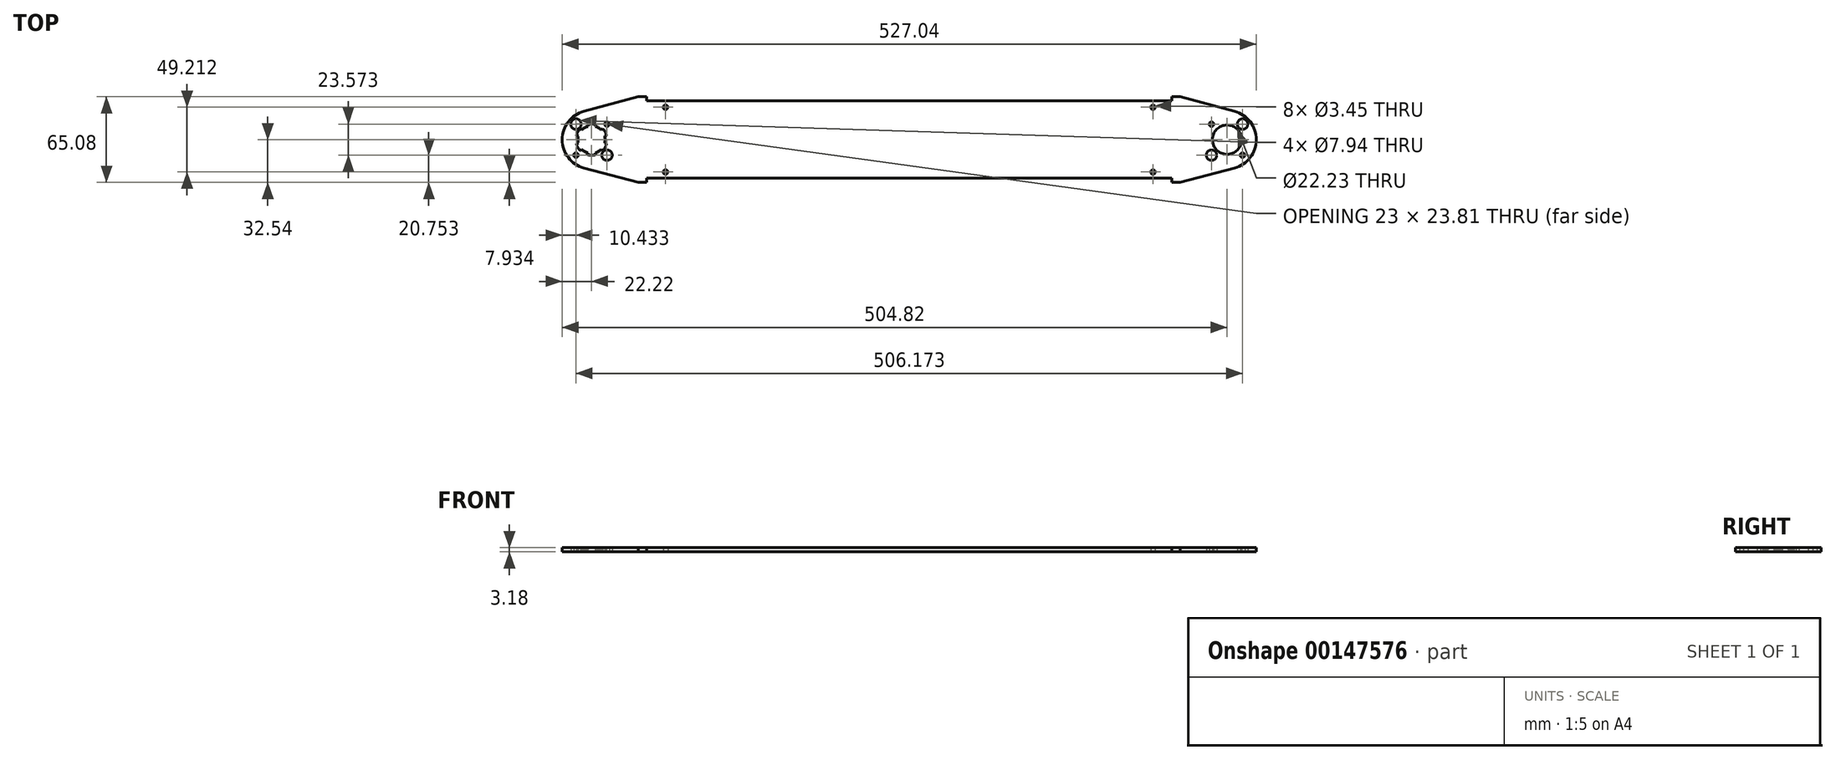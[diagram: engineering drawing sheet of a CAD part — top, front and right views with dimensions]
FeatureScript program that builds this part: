
annotation { "Feature Type Name" : "Feature", "Feature Type Description" : "" }
export const myFeature = defineFeature(function(context is Context, id is Id, definition is map)
    precondition{}
    {
        {
            var Q0;
            Q0=qCreatedBy(makeId("Top.planeOp"),FACE);
            var sketch = newSketch(context, id + "F0", { "sketchPlane" : qUnion([Q0])});
            skPoint(sketch, "E0.rect.middle", {"position": v(0, 0) * mm});
            skCircle(sketch, "E1", {"center": v(0, 0) * mm, "radius": 11.11 * mm});
            skLineSegment(sketch, "E2.bottom", {"start": v(11.79, 11.79) * mm, "end": v(-11.79, 11.79) * mm, "construction": true});
            skLineSegment(sketch, "E2.left", {"start": v(11.79, 11.79) * mm, "end": v(11.79, -11.79) * mm, "construction": true});
            skLineSegment(sketch, "E2.right", {"start": v(-11.79, 11.79) * mm, "end": v(-11.79, -11.79) * mm, "construction": true});
            skCircle(sketch, "E3", {"center": v(11.79, 11.79) * mm, "radius": 5.56 * mm, "construction": true});
            skCircle(sketch, "E4", {"center": v(-11.79, 11.79) * mm, "radius": 1.73 * mm});
            skCircle(sketch, "E5", {"center": v(11.79, 11.79) * mm, "radius": 3.97 * mm});
            skCircle(sketch, "E6", {"center": v(11.79, -11.79) * mm, "radius": 1.73 * mm});
            skCircle(sketch, "E7", {"center": v(-11.79, -11.79) * mm, "radius": 3.97 * mm});
            skArc(sketch, "E8", {"start": v(-488.35, 21.47) * mm, "mid": v(-504.83, 0) * mm, "end": v(-488.35, -21.47) * mm});
            skLineSegment(sketch, "E9.bottom", {"start": v(-494.39, 11.79) * mm, "end": v(-470.81, 11.79) * mm, "construction": true});
            skLineSegment(sketch, "E9.top", {"start": v(-494.39, -11.79) * mm, "end": v(-470.81, -11.79) * mm, "construction": true});
            skLineSegment(sketch, "E9.left", {"start": v(-494.39, 11.79) * mm, "end": v(-494.39, -11.79) * mm, "construction": true});
            skLineSegment(sketch, "E9.right", {"start": v(-470.81, 11.79) * mm, "end": v(-470.81, -11.79) * mm, "construction": true});
            skCircle(sketch, "E10", {"center": v(-470.81, 11.79) * mm, "radius": 1.73 * mm});
            skCircle(sketch, "E11", {"center": v(-482.6, 0) * mm, "radius": 10.32 * mm});
            skCircle(sketch, "E12", {"center": v(-494.39, 11.79) * mm, "radius": 3.97 * mm});
            skCircle(sketch, "E13", {"center": v(-494.39, -11.79) * mm, "radius": 1.73 * mm});
            skCircle(sketch, "E14", {"center": v(-470.81, -11.79) * mm, "radius": 3.97 * mm});
            skLineSegment(sketch, "E15", {"start": v(0, 0) * mm, "end": v(-482.6, 0) * mm, "construction": true});
            skLineSegment(sketch, "E16", {"start": v(-488.35, -21.47) * mm, "end": v(-447.02, -32.54) * mm});
            skLineSegment(sketch, "E17", {"start": v(-488.35, 21.47) * mm, "end": v(-447.02, 32.54) * mm});
            skLineSegment(sketch, "E18", {"start": v(-440.67, -29.37) * mm, "end": v(-41.93, -29.37) * mm});
            skLineSegment(sketch, "E19", {"start": v(-440.67, 29.37) * mm, "end": v(-41.93, 29.37) * mm});
            skLineSegment(sketch, "E20", {"start": v(-440.67, 32.54) * mm, "end": v(-440.67, 29.37) * mm});
            skLineSegment(sketch, "E21", {"start": v(-440.67, 32.54) * mm, "end": v(-447.02, 32.54) * mm});
            skLineSegment(sketch, "E22", {"start": v(-440.67, -29.37) * mm, "end": v(-440.67, -32.54) * mm});
            skLineSegment(sketch, "E23", {"start": v(-440.67, -32.54) * mm, "end": v(-447.02, -32.54) * mm});
            skLineSegment(sketch, "E24", {"start": v(-41.93, -29.37) * mm, "end": v(-41.93, -32.54) * mm});
            skLineSegment(sketch, "E25", {"start": v(-41.93, -32.54) * mm, "end": v(-35.58, -32.54) * mm});
            skLineSegment(sketch, "E26", {"start": v(-41.93, 29.37) * mm, "end": v(-41.93, 32.54) * mm});
            skLineSegment(sketch, "E27", {"start": v(-41.93, 32.54) * mm, "end": v(-35.58, 32.54) * mm});
            skLineSegment(sketch, "E28", {"start": v(-35.58, -32.54) * mm, "end": v(5.75, -21.47) * mm});
            skLineSegment(sketch, "E29", {"start": v(5.75, 21.47) * mm, "end": v(-35.58, 32.54) * mm});
            skArc(sketch, "E30", {"start": v(5.75, -21.47) * mm, "mid": v(22.23, 0) * mm, "end": v(5.75, 21.47) * mm});
            skLineSegment(sketch, "E31", {"start": v(-440.67, 29.37) * mm, "end": v(-440.67, 24.6) * mm, "construction": true});
            skLineSegment(sketch, "E32", {"start": v(-440.67, 24.6) * mm, "end": v(-426.38, 24.6) * mm, "construction": true});
            skLineSegment(sketch, "E33", {"start": v(-440.67, -29.37) * mm, "end": v(-440.67, -24.6) * mm, "construction": true});
            skLineSegment(sketch, "E34", {"start": v(-440.67, -24.6) * mm, "end": v(-426.38, -24.6) * mm, "construction": true});
            skLineSegment(sketch, "E35", {"start": v(-41.93, -29.37) * mm, "end": v(-41.93, -24.6) * mm, "construction": true});
            skLineSegment(sketch, "E36", {"start": v(-41.93, -24.6) * mm, "end": v(-56.22, -24.6) * mm, "construction": true});
            skLineSegment(sketch, "E37", {"start": v(-41.93, 29.37) * mm, "end": v(-41.93, 24.6) * mm, "construction": true});
            skLineSegment(sketch, "E38", {"start": v(-41.93, 24.6) * mm, "end": v(-56.22, 24.6) * mm, "construction": true});
            skCircle(sketch, "E39", {"center": v(-426.38, 24.6) * mm, "radius": 1.73 * mm});
            skCircle(sketch, "E40", {"center": v(-56.22, 24.6) * mm, "radius": 1.73 * mm});
            skCircle(sketch, "E41", {"center": v(-56.22, -24.6) * mm, "radius": 1.73 * mm});
            skCircle(sketch, "E42", {"center": v(-426.38, -24.6) * mm, "radius": 1.73 * mm});
            skLineSegment(sketch, "E43", {"start": v(-11.79, -11.79) * mm, "end": v(11.79, -11.79) * mm, "construction": true});
            skLineSegment(sketch, "E44", {"start": v(-241.3, -29.37) * mm, "end": v(-241.3, 0) * mm, "construction": true});
            skLineSegment(sketch, "E45", {"start": v(-241.3, 0) * mm, "end": v(-241.3, 29.37) * mm, "construction": true});
            skSolve(sketch);
        }
        {
            var Q0;
            Q0=qSketchRegion(id+"F0",true);
            extrude(context, id + "F1", {"entities" : qUnion([Q0]), "depth" : 3.17 * mm});
        }
        {
            var Q0;
            Q0=makeQuery(id+"F1.opExtrude","CAP_FACE",FACE,{"disambiguationData":[OSD([sQuery(id+"F0.wireOp",EDGE,"d63eafa0-1946-4b0e-8293-95e246b273c5.rect.bottom"),sQuery(id+"F0.wireOp",EDGE,"d63eafa0-1946-4b0e-8293-95e246b273c5.rect.top"),sQuery(id+"F0.wireOp",EDGE,"5983dcdd-59a7-4b72-80fd-e4567be1ae8a"),sQuery(id+"F0.wireOp",EDGE,"5a538b3e-fc2b-4d64-affd-5d60433388e5"),sQuery(id+"F0.wireOp",EDGE,"72e86de7-b207-474f-aadf-64543fae3f9b"),sQuery(id+"F0.wireOp",EDGE,"1c038800-5bd5-4753-8b38-6da13ef78ef9"),sQuery(id+"F0.wireOp",EDGE,"EbMUZoU6-Ffds-1dNq-SxhE-hPi8oSjhvaod"),sQuery(id+"F0.wireOp",EDGE,"RfgQjzcw-1Izs-lnTa-bWkk-oBHRDQjbZqQC"),sQuery(id+"F0.wireOp",EDGE,"1cCQAcjj-TyQA-3DMx-kDix-v5yZVaaGeXVM"),sQuery(id+"F0.wireOp",EDGE,"7KPu8lni-3ZWA-t6oJ-FRoh-C5MB3aVr7E9B"),sQuery(id+"F0.wireOp",EDGE,"bSzr06ES-7M0i-Fw5H-UJmt-4e4EQGRPIe4n"),sQuery(id+"F0.wireOp",EDGE,"WGsr6OjU-OX8l-mawA-7cCc-MfOuMOY06Cp5"),sQuery(id+"F0.wireOp",EDGE,"9mrz1cDN-18gM-20ra-6VCO-jp25g10tvNn2"),sQuery(id+"F0.wireOp",EDGE,"G0uOisy3-Mq6h-PcKh-Zkf4-CVoCvP3Hii1l"),sQuery(id+"F0.wireOp",EDGE,"1ae556be-0ab9-4322-b48e-98cf5a741ae0"),sQuery(id+"F0.wireOp",EDGE,"676cd913-43f8-42b3-8cdc-a90136d19ef5"),sQuery(id+"F0.wireOp",EDGE,"xnt2EyF8-ZVyQ-RbWD-GIsP-ThkcyX8ZioIH.bottom"),sQuery(id+"F0.wireOp",EDGE,"xnt2EyF8-ZVyQ-RbWD-GIsP-ThkcyX8ZioIH.top"),sQuery(id+"F0.wireOp",EDGE,"xnt2EyF8-ZVyQ-RbWD-GIsP-ThkcyX8ZioIH.left"),sQuery(id+"F0.wireOp",EDGE,"E1"),sQuery(id+"F0.wireOp",EDGE,"Jo9pZc7T-t0kF-vjz1-dNbX-L65bwNqtrrdz"),sQuery(id+"F0.wireOp",EDGE,"lEYoY9t7-PMOS-SVp6-xfnB-Xp9WdWMCDdum"),sQuery(id+"F0.wireOp",EDGE,"s7aM02SC-9XQ7-dueL-DqMg-ZFuJqOofj9mt"),sQuery(id+"F0.wireOp",EDGE,"deKa9ngt-XMq2-GGkr-SZIa-KlyN0U5bcCDe"),sQuery(id+"F0.wireOp",EDGE,"E4"),sQuery(id+"F0.wireOp",EDGE,"E5"),sQuery(id+"F0.wireOp",EDGE,"E6"),sQuery(id+"F0.wireOp",EDGE,"E7"),sQuery(id+"F0.wireOp",EDGE,"E8"),sQuery(id+"F0.wireOp",EDGE,"E10"),sQuery(id+"F0.wireOp",EDGE,"E11"),sQuery(id+"F0.wireOp",EDGE,"E12"),sQuery(id+"F0.wireOp",EDGE,"E13"),sQuery(id+"F0.wireOp",EDGE,"E14")])],"isStart":true});
            var sketch = newSketch(context, id + "F2", { "sketchPlane" : qUnion([Q0])});
            skLineSegment(sketch, "E46", {"start": v(-482.6, 0) * mm, "end": v(-491.54, -5.16) * mm, "construction": true});
            skArc(sketch, "E47", {"start": v(-492.57, -2.67) * mm, "mid": v(-491.54, -5.16) * mm, "end": v(-489.9, -7.3) * mm});
            skLineSegment(sketch, "E48", {"start": v(-482.6, 0) * mm, "end": v(-489.9, -7.3) * mm, "construction": true});
            skLineSegment(sketch, "E49", {"start": v(-482.6, 0) * mm, "end": v(-492.57, -2.67) * mm, "construction": true});
            skLineSegment(sketch, "E50", {"start": v(-489.9, -7.3) * mm, "end": v(-491.02, -8.42) * mm});
            skLineSegment(sketch, "E51", {"start": v(-492.57, -2.67) * mm, "end": v(-494.1, -3.08) * mm});
            skArc(sketch, "E52", {"start": v(-494.1, -3.08) * mm, "mid": v(-492.91, -5.95) * mm, "end": v(-491.02, -8.42) * mm});
            skLineSegment(sketch, "E53", {"start": v(-482.6, 0) * mm, "end": v(-492.92, 0) * mm, "construction": true});
            skSolve(sketch);
        }
        {
            var Q0;
            Q0=qSketchRegion(id+"F2",true);
            var Q1;
            Q1=makeQuery(id+"F1.opExtrude","CAP_FACE",FACE,{"disambiguationData":[OSD([sQuery(id+"F0.wireOp",EDGE,"d63eafa0-1946-4b0e-8293-95e246b273c5.rect.bottom"),sQuery(id+"F0.wireOp",EDGE,"d63eafa0-1946-4b0e-8293-95e246b273c5.rect.top"),sQuery(id+"F0.wireOp",EDGE,"5983dcdd-59a7-4b72-80fd-e4567be1ae8a"),sQuery(id+"F0.wireOp",EDGE,"5a538b3e-fc2b-4d64-affd-5d60433388e5"),sQuery(id+"F0.wireOp",EDGE,"72e86de7-b207-474f-aadf-64543fae3f9b"),sQuery(id+"F0.wireOp",EDGE,"1c038800-5bd5-4753-8b38-6da13ef78ef9"),sQuery(id+"F0.wireOp",EDGE,"EbMUZoU6-Ffds-1dNq-SxhE-hPi8oSjhvaod"),sQuery(id+"F0.wireOp",EDGE,"RfgQjzcw-1Izs-lnTa-bWkk-oBHRDQjbZqQC"),sQuery(id+"F0.wireOp",EDGE,"1cCQAcjj-TyQA-3DMx-kDix-v5yZVaaGeXVM"),sQuery(id+"F0.wireOp",EDGE,"7KPu8lni-3ZWA-t6oJ-FRoh-C5MB3aVr7E9B"),sQuery(id+"F0.wireOp",EDGE,"bSzr06ES-7M0i-Fw5H-UJmt-4e4EQGRPIe4n"),sQuery(id+"F0.wireOp",EDGE,"WGsr6OjU-OX8l-mawA-7cCc-MfOuMOY06Cp5"),sQuery(id+"F0.wireOp",EDGE,"9mrz1cDN-18gM-20ra-6VCO-jp25g10tvNn2"),sQuery(id+"F0.wireOp",EDGE,"G0uOisy3-Mq6h-PcKh-Zkf4-CVoCvP3Hii1l"),sQuery(id+"F0.wireOp",EDGE,"1ae556be-0ab9-4322-b48e-98cf5a741ae0"),sQuery(id+"F0.wireOp",EDGE,"676cd913-43f8-42b3-8cdc-a90136d19ef5"),sQuery(id+"F0.wireOp",EDGE,"xnt2EyF8-ZVyQ-RbWD-GIsP-ThkcyX8ZioIH.bottom"),sQuery(id+"F0.wireOp",EDGE,"xnt2EyF8-ZVyQ-RbWD-GIsP-ThkcyX8ZioIH.top"),sQuery(id+"F0.wireOp",EDGE,"xnt2EyF8-ZVyQ-RbWD-GIsP-ThkcyX8ZioIH.left"),sQuery(id+"F0.wireOp",EDGE,"E1"),sQuery(id+"F0.wireOp",EDGE,"Jo9pZc7T-t0kF-vjz1-dNbX-L65bwNqtrrdz"),sQuery(id+"F0.wireOp",EDGE,"lEYoY9t7-PMOS-SVp6-xfnB-Xp9WdWMCDdum"),sQuery(id+"F0.wireOp",EDGE,"s7aM02SC-9XQ7-dueL-DqMg-ZFuJqOofj9mt"),sQuery(id+"F0.wireOp",EDGE,"deKa9ngt-XMq2-GGkr-SZIa-KlyN0U5bcCDe"),sQuery(id+"F0.wireOp",EDGE,"E4"),sQuery(id+"F0.wireOp",EDGE,"E5"),sQuery(id+"F0.wireOp",EDGE,"E6"),sQuery(id+"F0.wireOp",EDGE,"E7"),sQuery(id+"F0.wireOp",EDGE,"E8"),sQuery(id+"F0.wireOp",EDGE,"E10"),sQuery(id+"F0.wireOp",EDGE,"E11"),sQuery(id+"F0.wireOp",EDGE,"E12"),sQuery(id+"F0.wireOp",EDGE,"E13"),sQuery(id+"F0.wireOp",EDGE,"E14")])],"isStart":false});
            extrude(context, id + "F3", {"entities" : qUnion([Q0]), "operationType" : NewBodyOperationType.REMOVE, "endBound" : BoundingType.UP_TO_SURFACE, "oppositeDirection" : true, "endBoundEntityFace" : qUnion([Q1]), "depth" : 25.4 * mm});
        }
        {
            var Q0;
            Q0=makeQuery(id+"F3.boolean.opBoolean","COPY",FACE,{"derivedFrom":makeQuery(id+"F3.opExtrude","SWEPT_FACE",FACE,{"disambiguationData":[OSD([sQuery(id+"F2.wireOp",EDGE,"E50")])]})});
            var Q1;
            Q1=makeQuery(id+"F3.boolean.opBoolean","COPY",FACE,{"derivedFrom":makeQuery(id+"F3.opExtrude","SWEPT_FACE",FACE,{"disambiguationData":[OSD([sQuery(id+"F2.wireOp",EDGE,"E52")])]})});
            var Q2;
            Q2=makeQuery(id+"F3.boolean.opBoolean","COPY",FACE,{"derivedFrom":makeQuery(id+"F3.opExtrude","SWEPT_FACE",FACE,{"disambiguationData":[OSD([sQuery(id+"F2.wireOp",EDGE,"E51")])]})});
            var Q3;
            Q3=makeQuery(id+"F1.opExtrude","SWEPT_FACE",FACE,{"disambiguationData":[OSD([sQuery(id+"F0.wireOp",EDGE,"E11")])]});
            circularPattern(context, id + "F4", {"patternType" : PatternType.FACE, "faces" : qUnion([Q0, Q1, Q2]), "axis" : qUnion([Q3]), "angle" : 60 * degree, "instanceCount" : 6});
        }
        {
            var Q0;
            Q0=makeQuery(id+"F1.opExtrude","CAP_FACE",FACE,{"disambiguationData":[OSD([sQuery(id+"F0.wireOp",EDGE,"E1"),sQuery(id+"F0.wireOp",EDGE,"E4"),sQuery(id+"F0.wireOp",EDGE,"E5"),sQuery(id+"F0.wireOp",EDGE,"E6"),sQuery(id+"F0.wireOp",EDGE,"E7"),sQuery(id+"F0.wireOp",EDGE,"E8"),sQuery(id+"F0.wireOp",EDGE,"E10"),sQuery(id+"F0.wireOp",EDGE,"E11"),sQuery(id+"F0.wireOp",EDGE,"E12"),sQuery(id+"F0.wireOp",EDGE,"E13"),sQuery(id+"F0.wireOp",EDGE,"E14"),sQuery(id+"F0.wireOp",EDGE,"E16"),sQuery(id+"F0.wireOp",EDGE,"E17"),sQuery(id+"F0.wireOp",EDGE,"E18"),sQuery(id+"F0.wireOp",EDGE,"E19"),sQuery(id+"F0.wireOp",EDGE,"E20"),sQuery(id+"F0.wireOp",EDGE,"E21"),sQuery(id+"F0.wireOp",EDGE,"E22"),sQuery(id+"F0.wireOp",EDGE,"E23"),sQuery(id+"F0.wireOp",EDGE,"E24"),sQuery(id+"F0.wireOp",EDGE,"E25"),sQuery(id+"F0.wireOp",EDGE,"E26"),sQuery(id+"F0.wireOp",EDGE,"E27"),sQuery(id+"F0.wireOp",EDGE,"E28"),sQuery(id+"F0.wireOp",EDGE,"E29"),sQuery(id+"F0.wireOp",EDGE,"E30"),sQuery(id+"F0.wireOp",EDGE,"E39"),sQuery(id+"F0.wireOp",EDGE,"VBQrvAlw-hTen-gxea-5rdB-eWDYfLApStqa"),sQuery(id+"F0.wireOp",EDGE,"yiHS12IZ-p0bI-Rr18-zCOr-yyMLVT9gFuvF"),sQuery(id+"F0.wireOp",EDGE,"E40"),sQuery(id+"F0.wireOp",EDGE,"E41"),sQuery(id+"F0.wireOp",EDGE,"rRnw4OZJ-V4Nv-Zfje-mNyT-Kr12XnqSrFdH"),sQuery(id+"F0.wireOp",EDGE,"E42"),sQuery(id+"F0.wireOp",EDGE,"j80b8Ypo-zIiU-stA5-HOYK-FsRsFb2xIukV")])],"isStart":true});
            var sketch = newSketch(context, id + "F5", { "sketchPlane" : qUnion([Q0])});
            skCircle(sketch, "E54", {"center": v(-482.6, 0) * mm, "radius": 11.11 * mm});
            skSolve(sketch);
        }
        {
            var Q0;
            Q0=qSketchRegion(id+"F5",true);
            extrude(context, id + "F6", {"entities" : qUnion([Q0]), "operationType" : NewBodyOperationType.REMOVE, "oppositeDirection" : true, "depth" : 1.95 * mm});
        }
    });
